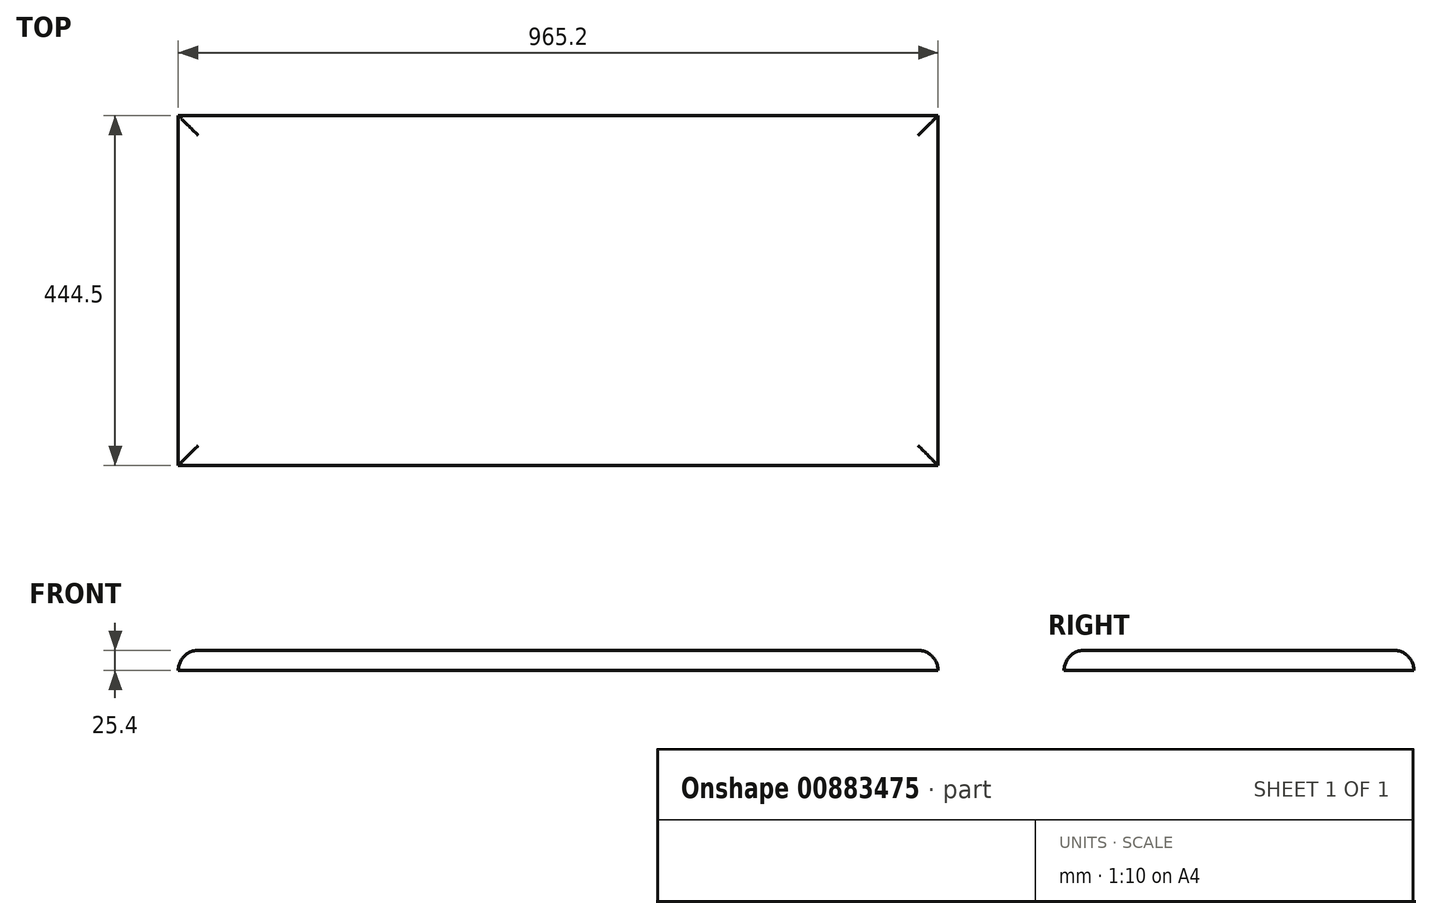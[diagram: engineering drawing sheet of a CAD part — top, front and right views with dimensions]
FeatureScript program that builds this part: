
annotation { "Feature Type Name" : "Feature", "Feature Type Description" : "" }
export const myFeature = defineFeature(function(context is Context, id is Id, definition is map)
    precondition{}
    {
        {
            var Q0;
            Q0=qCreatedBy(makeId("Top.planeOp"),FACE);
            var sketch = newSketch(context, id + "F0", { "sketchPlane" : qUnion([Q0])});
            skLineSegment(sketch, "E0.bottom", {"start": v(0, 0) * mm, "end": v(965.2, 0) * mm});
            skLineSegment(sketch, "E0.top", {"start": v(0, 444.5) * mm, "end": v(965.2, 444.5) * mm});
            skLineSegment(sketch, "E0.left", {"start": v(0, 0) * mm, "end": v(0, 444.5) * mm});
            skLineSegment(sketch, "E0.right", {"start": v(965.2, 0) * mm, "end": v(965.2, 444.5) * mm});
            skSolve(sketch);
        }
        {
            var Q0;
            Q0 = qSketchRegion(id + "F0", true);
            extrude(context, id + "F1", {"entities" : qUnion([Q0]), "depth" : 25.4 * mm, "offsetDistance" : 25.4 * mm});
        }
        {
            var Q0;
            Q0=qCreatedBy(makeId("Right.planeOp"),FACE);
            var sketch = newSketch(context, id + "F2", { "sketchPlane" : qUnion([Q0])});
            skArc(sketch, "E1", {"start": v(25.4, 25.4) * mm, "mid": v(7.44, 17.96) * mm, "end": v(0, 0) * mm});
            skLineSegment(sketch, "E2", {"start": v(25.4, 25.4) * mm, "end": v(0, 25.4) * mm});
            skLineSegment(sketch, "E3", {"start": v(0, 25.4) * mm, "end": v(0, 0) * mm});
            skSolve(sketch);
        }
        {
            var Q0;
            Q0=makeQuery(id+"F2.imprint","IMPRINT",FACE,{"disambiguationData":[TD([[makeQuery(id+"F2.imprint","IMPRINT",EDGE,{"derivedFrom":sQuery(id+"F2.wireOp",EDGE,"E1")}),-1.0]])]});
            var Q1;
            Q1=makeQuery(id+"F1.opExtrude","CAP_EDGE",EDGE,{"disambiguationData":[OSD([sQuery(id+"F0.wireOp",EDGE,"E0.bottom")])],"isStart":false});
            var Q2;
            Q2=makeQuery(id+"F1.opExtrude","CAP_EDGE",EDGE,{"disambiguationData":[OSD([sQuery(id+"F0.wireOp",EDGE,"E0.right")])],"isStart":false});
            var Q3;
            Q3=makeQuery(id+"F1.opExtrude","CAP_EDGE",EDGE,{"disambiguationData":[OSD([sQuery(id+"F0.wireOp",EDGE,"E0.top")])],"isStart":false});
            var Q4;
            Q4=makeQuery(id+"F1.opExtrude","CAP_EDGE",EDGE,{"disambiguationData":[OSD([sQuery(id+"F0.wireOp",EDGE,"E0.left")])],"isStart":false});
            sweep(context, id + "F3", {"operationType" : NewBodyOperationType.REMOVE, "profiles" : qUnion([Q0]), "path" : qUnion([Q1, Q2, Q3, Q4])});
        }
    });
